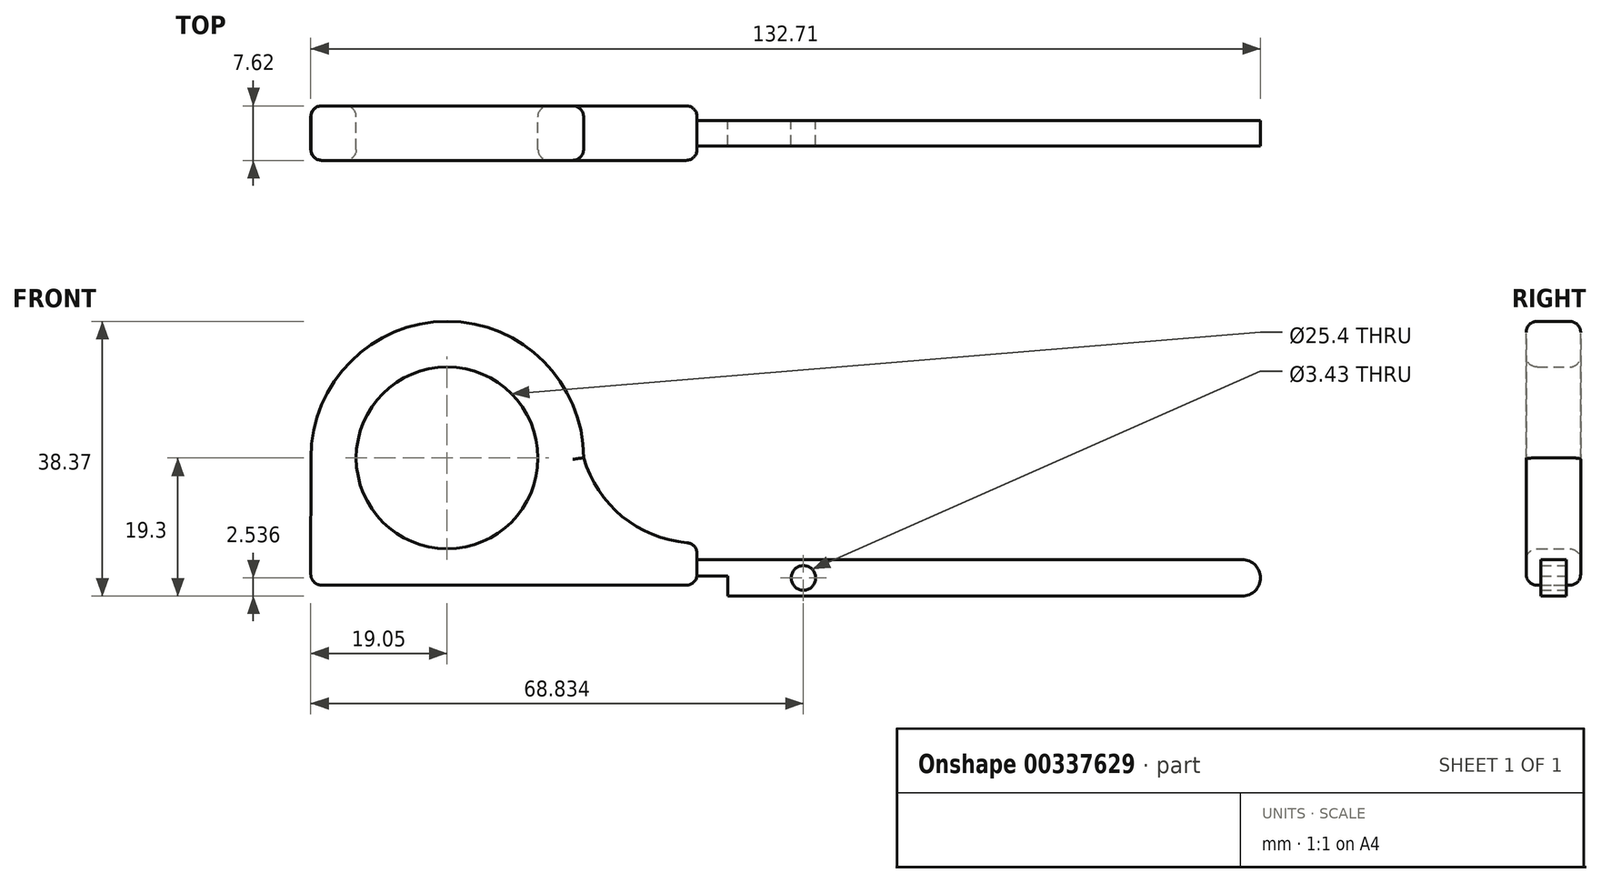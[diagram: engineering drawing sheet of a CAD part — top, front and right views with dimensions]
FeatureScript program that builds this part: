
annotation { "Feature Type Name" : "Feature", "Feature Type Description" : "" }
export const myFeature = defineFeature(function(context is Context, id is Id, definition is map)
    precondition{}
    {
        {
            var Q0;
            Q0=qCreatedBy(makeId("Front.planeOp"),FACE);
            var sketch = newSketch(context, id + "F0", { "sketchPlane" : qUnion([Q0])});
            skLineSegment(sketch, "E0", {"start": v(-19.05, -17.78) * mm, "end": v(-19.04, 0.02) * mm});
            skLineSegment(sketch, "E1.left", {"start": v(-19.05, -17.78) * mm, "end": v(-19.05, 0) * mm});
            skLineSegment(sketch, "E2.left", {"start": v(34.93, -17.78) * mm, "end": v(34.93, -11.91) * mm});
            skArc(sketch, "E3", {"start": v(19.06, 0.02) * mm, "mid": v(25, -8.6) * mm, "end": v(34.92, -11.91) * mm});
            skCircle(sketch, "E4", {"center": v(0, 0) * mm, "radius": 12.7 * mm});
            skArc(sketch, "E5", {"start": v(19.06, 0.02) * mm, "mid": v(0.01, 19.07) * mm, "end": v(-19.04, 0.02) * mm});
            skLineSegment(sketch, "E6", {"start": v(-19.05, -17.78) * mm, "end": v(34.93, -17.78) * mm});
            skLineSegment(sketch, "E7.bottom", {"start": v(111.12, -14.22) * mm, "end": v(34.92, -14.22) * mm});
            skArc(sketch, "E8", {"start": v(111.12, -19.3) * mm, "mid": v(113.66, -16.76) * mm, "end": v(111.12, -14.22) * mm});
            skLineSegment(sketch, "E9.bottom", {"start": v(34.93, -14.22) * mm, "end": v(34.92, -14.22) * mm});
            skLineSegment(sketch, "E9.top", {"start": v(39.24, -16.5) * mm, "end": v(34.93, -16.5) * mm});
            skLineSegment(sketch, "E9.right", {"start": v(34.93, -14.22) * mm, "end": v(34.93, -16.5) * mm});
            skCircle(sketch, "E10", {"center": v(49.78, -16.76) * mm, "radius": 1.71 * mm});
            skLineSegment(sketch, "E11", {"start": v(111.12, -19.3) * mm, "end": v(39.24, -19.3) * mm});
            skLineSegment(sketch, "E12", {"start": v(39.24, -19.3) * mm, "end": v(39.24, -16.5) * mm});
            skSolve(sketch);
        }
        {
            var Q0;
            Q0=makeQuery(id+"F0.imprint","IMPRINT",FACE,{"disambiguationData":[TD([[makeQuery(id+"F0.imprint","IMPRINT",EDGE,{"derivedFrom":sQuery(id+"F0.wireOp",EDGE,"E7.bottom")}),1.0]])]});
            extrude(context, id + "F1", {"entities" : qUnion([Q0]), "endBound" : BoundingType.SYMMETRIC, "depth" : 3.56 * mm});
        }
        {
            var Q0;
            Q0=makeQuery(id+"F0.imprint","IMPRINT",FACE,{"disambiguationData":[TD([[makeQuery(id+"F0.imprint","IMPRINT",EDGE,{"derivedFrom":sQuery(id+"F0.wireOp",EDGE,"E0")}),-1.0]])]});
            extrude(context, id + "F2", {"entities" : qUnion([Q0]), "endBound" : BoundingType.SYMMETRIC, "depth" : 7.62 * mm});
        }
        {
            var Q0;
            Q0=makeQuery(id+"F2.opExtrude","CAP_FACE",FACE,{"disambiguationData":[OSD([sQuery(id+"F0.wireOp",EDGE,"E0"),sQuery(id+"F0.wireOp",EDGE,"E2.left"),sQuery(id+"F0.wireOp",EDGE,"E3"),sQuery(id+"F0.wireOp",EDGE,"E4"),sQuery(id+"F0.wireOp",EDGE,"E5"),sQuery(id+"F0.wireOp",EDGE,"E6"),sQuery(id+"F0.wireOp",EDGE,"E9.right")])],"isStart":false});
            var Q1;
            Q1=makeQuery(id+"F2.opExtrude","CAP_FACE",FACE,{"disambiguationData":[OSD([sQuery(id+"F0.wireOp",EDGE,"E0"),sQuery(id+"F0.wireOp",EDGE,"E2.left"),sQuery(id+"F0.wireOp",EDGE,"E3"),sQuery(id+"F0.wireOp",EDGE,"E4"),sQuery(id+"F0.wireOp",EDGE,"E5"),sQuery(id+"F0.wireOp",EDGE,"E6"),sQuery(id+"F0.wireOp",EDGE,"E9.right")])],"isStart":true});
            var Q2;
            Q2=makeQuery(id+"F2.opExtrude","SWEPT_FACE",FACE,{"disambiguationData":[OSD([sQuery(id+"F0.wireOp",EDGE,"E2.left"),sQuery(id+"F0.wireOp",EDGE,"E9.right")])]});
            var Q3;
            Q3=makeQuery(id+"F2.opExtrude","SWEPT_FACE",FACE,{"disambiguationData":[OSD([sQuery(id+"F0.wireOp",EDGE,"E6")])]});
            fillet(context, id + "F3", {"entities" : qUnion([Q0, Q1, Q2, Q3]), "radius" : 1.52 * mm, "tangentPropagation" : true, "allowEdgeOverflow" : false});
        }
    });
